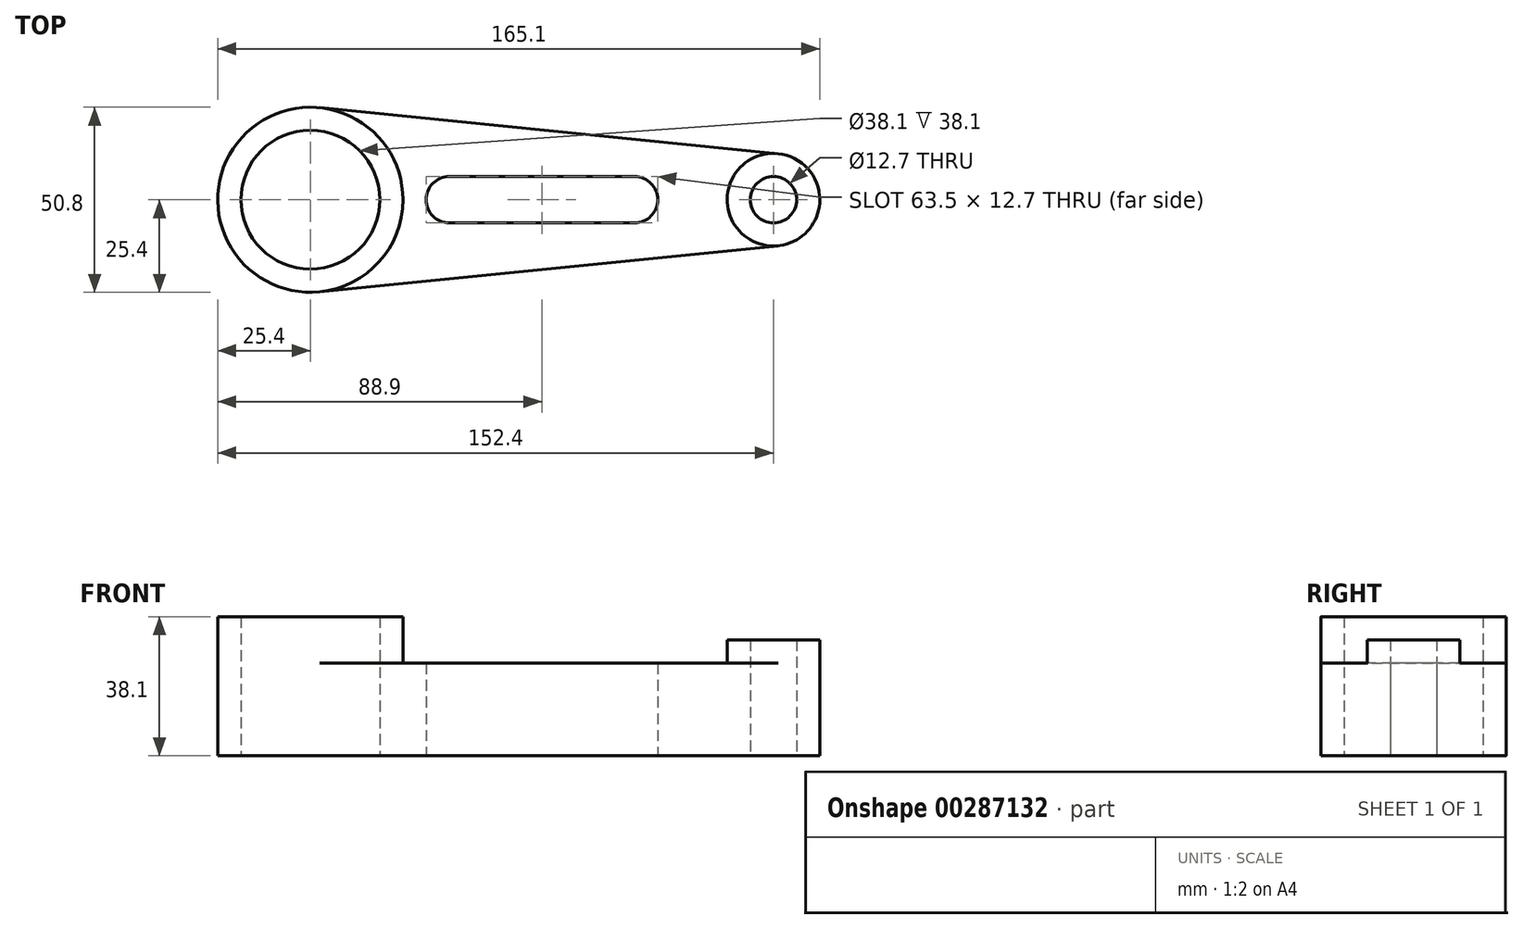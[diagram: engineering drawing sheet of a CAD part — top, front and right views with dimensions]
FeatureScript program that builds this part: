
annotation { "Feature Type Name" : "Feature", "Feature Type Description" : "" }
export const myFeature = defineFeature(function(context is Context, id is Id, definition is map)
    precondition{}
    {
        {
            var Q0;
            Q0=qCreatedBy(makeId("Top.planeOp"),FACE);
            var sketch = newSketch(context, id + "F0", { "sketchPlane" : qUnion([Q0])});
            skArc(sketch, "E0", {"start": v(0, 6.35) * mm, "mid": v(-6.35, 0) * mm, "end": v(0, -6.35) * mm});
            skArc(sketch, "E1", {"start": v(50.8, -6.35) * mm, "mid": v(57.15, 0) * mm, "end": v(50.8, 6.35) * mm});
            skCircle(sketch, "E2", {"center": v(-38.1, 0) * mm, "radius": 19.05 * mm});
            skCircle(sketch, "E3", {"center": v(-38.1, 0) * mm, "radius": 25.4 * mm});
            skCircle(sketch, "E4", {"center": v(88.9, 0) * mm, "radius": 6.35 * mm});
            skCircle(sketch, "E5", {"center": v(88.9, 0) * mm, "radius": 12.7 * mm});
            skPoint(sketch, "E6", {"position": v(0, 6.35) * mm});
            skPoint(sketch, "E7", {"position": v(0, -6.35) * mm});
            skPoint(sketch, "E8", {"position": v(50.8, 6.35) * mm});
            skPoint(sketch, "E9", {"position": v(50.8, -6.35) * mm});
            skLineSegment(sketch, "E10", {"start": v(0, 6.35) * mm, "end": v(50.8, 6.35) * mm});
            skLineSegment(sketch, "E11", {"start": v(0, -6.35) * mm, "end": v(50.8, -6.35) * mm});
            skLineSegment(sketch, "E12", {"start": v(-35.56, -25.27) * mm, "end": v(90.17, -12.64) * mm});
            skLineSegment(sketch, "E13", {"start": v(-35.56, 25.27) * mm, "end": v(90.17, 12.64) * mm});
            skSolve(sketch);
        }
        {
            var Q0;
            Q0=makeQuery(id+"F0.imprint","IMPRINT",FACE,{"disambiguationData":[TD([[makeQuery(id+"F0.imprint","IMPRINT",EDGE,{"derivedFrom":sQuery(id+"F0.wireOp",EDGE,"E0")}),-1.0]])]});
            extrude(context, id + "F1", {"entities" : qUnion([Q0]), "depth" : 25.4 * mm});
        }
        {
            var Q0;
            Q0=makeQuery(id+"F0.imprint","IMPRINT",FACE,{"disambiguationData":[TD([[makeQuery(id+"F0.imprint","IMPRINT",EDGE,{"derivedFrom":sQuery(id+"F0.wireOp",EDGE,"E2")}),-1.0]])]});
            extrude(context, id + "F2", {"entities" : qUnion([Q0]), "operationType" : NewBodyOperationType.ADD, "depth" : 38.1 * mm});
        }
        {
            var Q0;
            Q0=makeQuery(id+"F0.imprint","IMPRINT",FACE,{"disambiguationData":[TD([[makeQuery(id+"F0.imprint","IMPRINT",EDGE,{"derivedFrom":sQuery(id+"F0.wireOp",EDGE,"E4")}),-1.0]])]});
            extrude(context, id + "F3", {"entities" : qUnion([Q0]), "operationType" : NewBodyOperationType.ADD, "depth" : 31.75 * mm});
        }
    });
